# Revit family: EN - MT 1840
name_source: partatom
category: Equipement spécialisé
units: mm (PartAtom-declared; Revit-internal decimal feet)

## family parameters
Basée sur le plan de construction = Non
Cote de connecteur circulaire = Utiliser le diamètre
Couper avec des vides une fois chargée = Non
Numéro OmniClass = 23.50.30.00
Partagée = Non
Point de calcul de pièce = Non
Titre OmniClass = Materials Handling
Toujours verticalement = Oui
Type d'élément = Normal

## types (1)
- MT 1840
    Average consumption (L/h) = 7.31
    CO2 emissions = 14.86
    Commentaires du type = Télescopique fixe grande hauteur
    Créé par = ATLANCAD
    Elévation par défaut = 0.00 m
    Engine norm = Stage V
    External turning radius over tyres = 3.07 m
    Fabricant = MANITOU
    Ground clearance = 0.37 m
    I.C. Engine power rating - Power (ch) = 100
    I.C. Engine power rating - Power (kW) = 75
    Max. capacity = 4000.00 kg
    Max. lifting height = 17.55 m
    Max. outreach = 13.08 m
    Modèle = MT 1840
    Noise at driving position (LpA) in dB(A) = 78
    Noise to environment (LwA) = 103
    Overall height = 2.50 m
    Overall length to carriage = 6.27 m
    Overall width = 2.42 m
    Tilt-down angle = 114.00°
    Tilt-up angle = 12.00°
    URL = www.manitou.com
    Unladen weight (with forks) = 11870.00 kg
    Wheelbase = 4.01 m
